# Revit family: LIXIL - EL-1000 - COBRA COBRATRON BASIN TAP TOUCHLESS _ FACE BASED
name_source: partatom
category: Plumbing Fixtures
units: mm (PartAtom-declared; Revit-internal decimal feet)

## family parameters
Cut with Voids When Loaded = No
Enable Cutting in Views = Yes
Host = Face
Maintain Annotation Orientation = No
OmniClass Number = 23.45.00.00
OmniClass Title = Sanitary, Laundry, and Cleaning Equipment
Part Type = Normal
Room Calculation Point = No
Round Connector Dimension = Use Diameter
Shared = Yes

## types (1)
- EL-1000
    Default Elevation = 1219 mm
    Description = Cobra EL-100 electronic no touch sensor mixer to sanware schedule and spec. Available from Lixil.
    Hosted on lixil.co.za = https://www.lixil.co.za
    M _ MIXER BODY = M _ LIXIL - CHROME 01
    M _ MIXER INDICATOR 01 = M _ LIXIL - INFRARED INDICATOR 01 - RED
    M _ MIXER RUBBER = M _ LIXIL - RUBBER - BLACK 01
    Product Specification = Supplier: Lixil.
Product Description: Jaswic Approved. Made of Dezincification resistant brass(DZR). Pillar type. Touch free. Single temperature, cold or blended water (suggested using EL-X60 (not included)). 4 x AA batteries included < 10 000 hours & G1/2 F X G1/2 F braided flexi connector hose required, not included.
2 Year Warranty Cobra EcoMind Cobra Genuine Cobra PureShine 
Product Code: FELMX1CC-0GT01.
SKU Code: EL-1000.
Barcode: 6002194032618.
Brand: Cobra
Range: Cobratron.
Category: Plumbing Supplies
Sub-Category: Electronic Taps
Colour: DZR Brass
Package Height: 80 mm
Package Width: 230 mm
Package Length: 280 mm
Package Volume: 5152000 mm³
Package Weight: 1.9 kg

Notes:
- Refer to manufacturer's and supplier's installation, maintenance and cleaning manual.
- Refer to manufacturer's and supplier's guarantees and warrantees document.

## geometry (parser evidence)
native form markers: Sweep x5
no freeform markers — native parametric forms only
